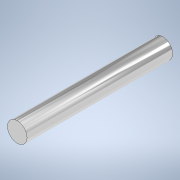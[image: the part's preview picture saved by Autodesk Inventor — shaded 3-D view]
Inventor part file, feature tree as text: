
AUTODESK INVENTOR PART (.ipt)
format: ipt  version: 2022 (Build 260153000, 153)  size: 97,792 bytes
history: native  units: mm
features: extrude x1, sketch x1
ambient origin geometry x8: Origin, YZ Plane, XZ Plane, XY Plane, X Axis, Y Axis, Z Axis, Center Point
bodies: Solid1 (feature_tree)
feature tree (2):
  extrude  "Extrusion1"  Depth=40.0mm TaperAngle=0.0deg
  sketch  "Sketch1"  dims[d0=5.4mm d1=40.0mm d2=0.0mm]
